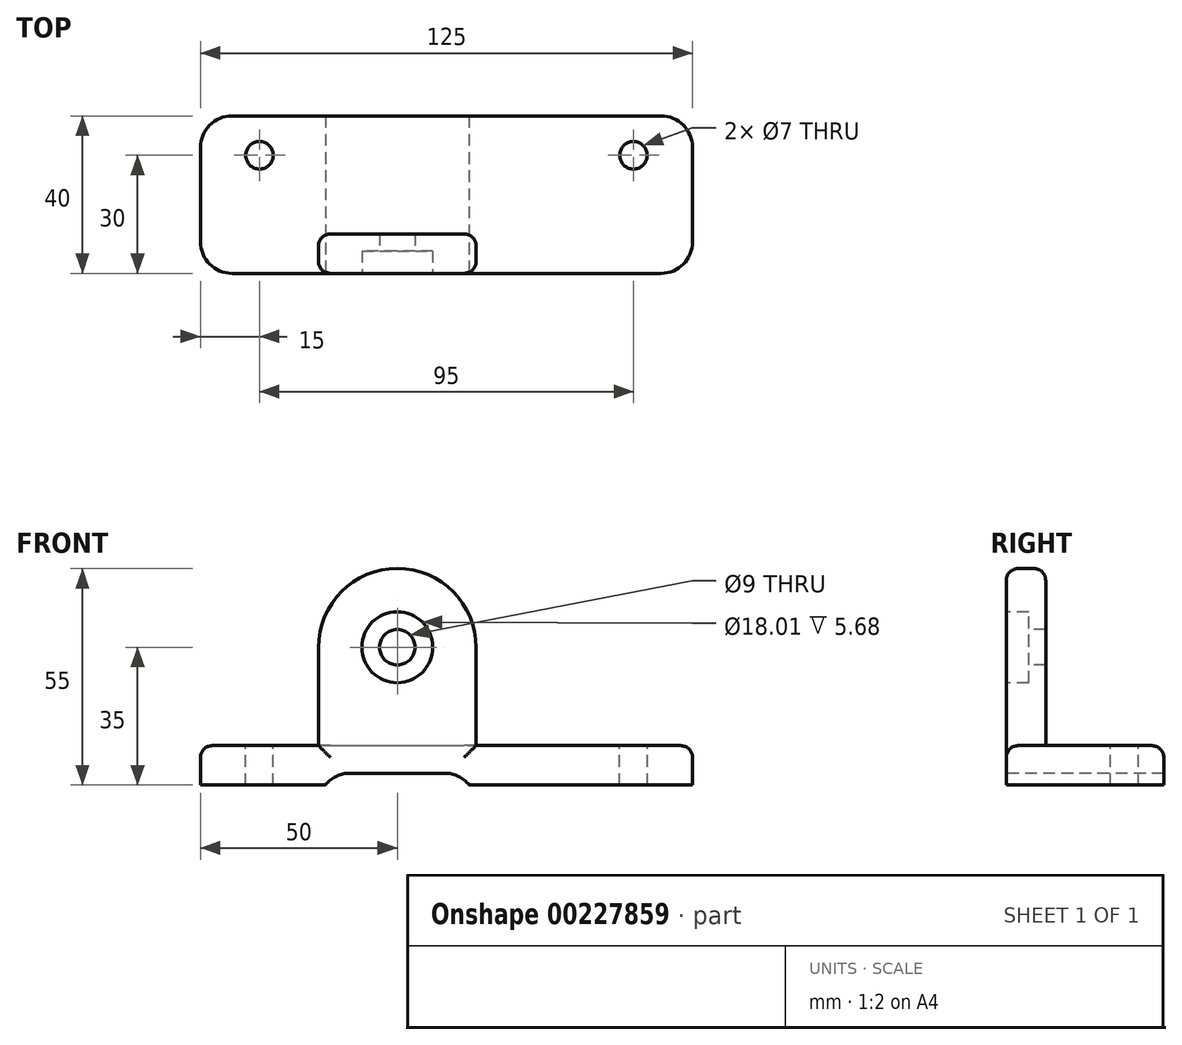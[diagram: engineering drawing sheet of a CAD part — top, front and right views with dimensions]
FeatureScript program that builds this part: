
annotation { "Feature Type Name" : "Feature", "Feature Type Description" : "" }
export const myFeature = defineFeature(function(context is Context, id is Id, definition is map)
    precondition{}
    {
        {
            var Q0;
            Q0=qCreatedBy(makeId("Top.planeOp"),FACE);
            var sketch = newSketch(context, id + "F0", { "sketchPlane" : qUnion([Q0])});
            skLineSegment(sketch, "E0.bottom", {"start": v(-62.5, 0) * mm, "end": v(62.5, 0) * mm});
            skLineSegment(sketch, "E0.top", {"start": v(-62.5, -40) * mm, "end": v(62.5, -40) * mm});
            skLineSegment(sketch, "E0.left", {"start": v(-62.5, 0) * mm, "end": v(-62.5, -40) * mm});
            skLineSegment(sketch, "E0.right", {"start": v(62.5, 0) * mm, "end": v(62.5, -40) * mm});
            skSolve(sketch);
        }
        {
            var Q0;
            Q0=makeQuery(id+"F0.imprint","IMPRINT",FACE,{"disambiguationData":[TD([[makeQuery(id+"F0.imprint","IMPRINT",EDGE,{"derivedFrom":sQuery(id+"F0.wireOp",EDGE,"E0.bottom")}),-1.0]])]});
            extrude(context, id + "F1", {"entities" : qUnion([Q0]), "depth" : 10 * mm});
        }
        {
            var Q0;
            Q0=makeQuery(id+"F1.opExtrude","SWEPT_FACE",FACE,{"disambiguationData":[OSD([sQuery(id+"F0.wireOp",EDGE,"E0.top")])]});
            var sketch = newSketch(context, id + "F2", { "sketchPlane" : qUnion([Q0])});
            skPoint(sketch, "E1.centerSnap0", {"position": v(0, 10) * mm});
            skArc(sketch, "E2", {"start": v(7.5, 35) * mm, "mid": v(-12.5, 55) * mm, "end": v(-32.5, 35) * mm});
            skLineSegment(sketch, "E3", {"start": v(-32.5, 35) * mm, "end": v(-32.5, 10) * mm});
            skLineSegment(sketch, "E4", {"start": v(7.5, 35) * mm, "end": v(7.5, 10) * mm});
            skLineSegment(sketch, "E5", {"start": v(7.5, 10) * mm, "end": v(-32.5, 10) * mm});
            skSolve(sketch);
        }
        {
            var Q0;
            Q0=makeQuery(id+"F2.imprint","IMPRINT",FACE,{"disambiguationData":[TD([[makeQuery(id+"F2.imprint","IMPRINT",EDGE,{"derivedFrom":sQuery(id+"F2.wireOp",EDGE,"E2")}),1.0]])]});
            extrude(context, id + "F3", {"entities" : qUnion([Q0]), "operationType" : NewBodyOperationType.ADD, "oppositeDirection" : true, "depth" : 10 * mm});
        }
        {
            var Q0;
            Q0=makeQuery(id+"F3.boolean.opBoolean","MERGE",FACE,{"derivedFrom":[makeQuery(id+"F1.opExtrude","SWEPT_FACE",FACE,{"disambiguationData":[OSD([sQuery(id+"F0.wireOp",EDGE,"E0.top")])]}),makeQuery(id+"F3.opExtrude","CAP_FACE",FACE,{"disambiguationData":[OSD([sQuery(id+"F2.wireOp",EDGE,"E2"),sQuery(id+"F2.wireOp",EDGE,"E3"),sQuery(id+"F2.wireOp",EDGE,"E4"),sQuery(id+"F2.wireOp",EDGE,"E5")])],"isStart":true})]});
            var sketch = newSketch(context, id + "F4", { "sketchPlane" : qUnion([Q0])});
            skPoint(sketch, "E6", {"position": v(-12.5, 35) * mm});
            skPoint(sketch, "E6.positionSnap0", {"position": v(-12.5, 55) * mm});
            skSolve(sketch);
        }
        {
            var Q0;
            Q0=sQuery(id+"F4.wireOp",VERTEX,"E6");
            var Q1;
            Q1=makeQuery(id+"F1.opExtrude","SWEPT_BODY",BODY,{"disambiguationData":[OSD([sQuery(id+"F0.wireOp",EDGE,"E0.bottom"),sQuery(id+"F0.wireOp",EDGE,"E0.top"),sQuery(id+"F0.wireOp",EDGE,"E0.left"),sQuery(id+"F0.wireOp",EDGE,"E0.right")])]});
            hole(context, id + "F5", {"style" : HoleStyle.C_BORE, "endStyle" : HoleEndStyle.THROUGH, "holeDiameter" : 9 * mm, "cBoreDiameter" : 18.01 * mm, "cBoreDepth" : 5.68 * mm, "locations" : qUnion([Q0]), "scope" : qUnion([Q1]), "isTappedThrough" : true});
        }
        {
            var Q0;
            Q0=makeQuery(id+"F1.opExtrude","CAP_FACE",FACE,{"disambiguationData":[OSD([sQuery(id+"F0.wireOp",EDGE,"E0.bottom"),sQuery(id+"F0.wireOp",EDGE,"E0.top"),sQuery(id+"F0.wireOp",EDGE,"E0.left"),sQuery(id+"F0.wireOp",EDGE,"E0.right")])],"isStart":false});
            var sketch = newSketch(context, id + "F6", { "sketchPlane" : qUnion([Q0])});
            skPoint(sketch, "E7", {"position": v(-47.5, -10) * mm});
            skPoint(sketch, "E8", {"position": v(103.03, -7.46) * mm});
            skPoint(sketch, "E9", {"position": v(47.5, -10) * mm});
            skSolve(sketch);
        }
        {
            var Q0;
            Q0=sQuery(id+"F6.wireOp",VERTEX,"E7");
            var Q1;
            Q1=sQuery(id+"F6.wireOp",VERTEX,"E9");
            var Q2;
            Q2=makeQuery(id+"F1.opExtrude","SWEPT_BODY",BODY,{"disambiguationData":[OSD([sQuery(id+"F0.wireOp",EDGE,"E0.bottom"),sQuery(id+"F0.wireOp",EDGE,"E0.top"),sQuery(id+"F0.wireOp",EDGE,"E0.left"),sQuery(id+"F0.wireOp",EDGE,"E0.right")])]});
            hole(context, id + "F7", {"style" : HoleStyle.SIMPLE, "endStyle" : HoleEndStyle.THROUGH, "holeDiameter" : 7 * mm, "locations" : qUnion([Q0, Q1]), "scope" : qUnion([Q2]), "isTappedThrough" : true});
        }
        {
            var Q0;
            Q0=makeQuery(id+"F3.boolean.opBoolean","MERGE",FACE,{"derivedFrom":[makeQuery(id+"F1.opExtrude","SWEPT_FACE",FACE,{"disambiguationData":[OSD([sQuery(id+"F0.wireOp",EDGE,"E0.top")])]}),makeQuery(id+"F3.opExtrude","CAP_FACE",FACE,{"disambiguationData":[OSD([sQuery(id+"F2.wireOp",EDGE,"E2"),sQuery(id+"F2.wireOp",EDGE,"E3"),sQuery(id+"F2.wireOp",EDGE,"E4"),sQuery(id+"F2.wireOp",EDGE,"E5")])],"isStart":true})]});
            var sketch = newSketch(context, id + "F8", { "sketchPlane" : qUnion([Q0])});
            skLineSegment(sketch, "E10.bottom", {"start": v(-32.5, 0) * mm, "end": v(7.5, 0) * mm});
            skLineSegment(sketch, "E10.top", {"start": v(-24.5, 3) * mm, "end": v(-0.5, 3) * mm});
            skLineSegment(sketch, "E10.left", {"start": v(-32.5, -5) * mm, "end": v(-32.5, 0) * mm});
            skLineSegment(sketch, "E10.right", {"start": v(7.5, -5) * mm, "end": v(7.5, 0) * mm});
            skPoint(sketch, "E11.visualSharp", {"position": v(-32.5, 3) * mm});
            skArc(sketch, "E11.filletArc", {"start": v(-24.5, 3) * mm, "mid": v(-30.16, 0.66) * mm, "end": v(-32.5, -5) * mm});
            skPoint(sketch, "E12.visualSharp", {"position": v(7.5, 3) * mm});
            skArc(sketch, "E12.filletArc", {"start": v(7.5, -5) * mm, "mid": v(5.16, 0.66) * mm, "end": v(-0.5, 3) * mm});
            skSolve(sketch);
        }
        {
            var Q0;
            {var subQ5=sQuery(id+"F8.wireOp",EDGE,"E10.top");Q0=makeQuery(id+"F8.imprint","IMPRINT",FACE,{"disambiguationData":[TD([[makeQuery(id+"F8.imprint","IMPRINT",EDGE,{"derivedFrom":subQ5}),-1.0]])]});}
            extrude(context, id + "F9", {"entities" : qUnion([Q0]), "operationType" : NewBodyOperationType.REMOVE, "oppositeDirection" : true, "depth" : 40 * mm});
        }
        {
            var Q0;
            Q0=makeQuery(id+"F1.opExtrude","SWEPT_EDGE",EDGE,{"disambiguationData":[OSD([sQuery(id+"F0.wireOp",EDGE,"E0.top"),sQuery(id+"F0.wireOp",EDGE,"E0.right")])]});
            var Q1;
            Q1=makeQuery(id+"F1.opExtrude","SWEPT_EDGE",EDGE,{"disambiguationData":[OSD([sQuery(id+"F0.wireOp",EDGE,"E0.bottom"),sQuery(id+"F0.wireOp",EDGE,"E0.right")])]});
            var Q2;
            Q2=makeQuery(id+"F1.opExtrude","SWEPT_EDGE",EDGE,{"disambiguationData":[OSD([sQuery(id+"F0.wireOp",EDGE,"E0.bottom"),sQuery(id+"F0.wireOp",EDGE,"E0.left")])]});
            var Q3;
            Q3=makeQuery(id+"F1.opExtrude","SWEPT_EDGE",EDGE,{"disambiguationData":[OSD([sQuery(id+"F0.wireOp",EDGE,"E0.top"),sQuery(id+"F0.wireOp",EDGE,"E0.left")])]});
            fillet(context, id + "F10", {"entities" : qUnion([Q0, Q1, Q2, Q3]), "radius" : 8 * mm, "tangentPropagation" : true, "allowEdgeOverflow" : false});
        }
        {
            var Q0;
            {var subQ1=sQuery(id+"F0.wireOp",EDGE,"E0.left");var subQ2=sQuery(id+"F0.wireOp",EDGE,"E0.top");Q0=makeQuery(id+"F3.boolean.opBoolean","SPLIT",EDGE,{"disambiguationData":[TD([makeQuery(id+"F1.opExtrude","SWEPT_FACE",FACE,{"disambiguationData":[OSD([subQ1])]})])],"derivedFrom":makeQuery(id+"F1.opExtrude","CAP_EDGE",EDGE,{"disambiguationData":[OSD([subQ2])],"isStart":false})});}
            var Q1;
            Q1=makeQuery(id+"F3.opExtrude","CAP_EDGE",EDGE,{"disambiguationData":[OSD([sQuery(id+"F2.wireOp",EDGE,"E4")])],"isStart":true});
            var Q2;
            Q2=makeQuery(id+"F3.opExtrude","CAP_EDGE",EDGE,{"disambiguationData":[OSD([sQuery(id+"F2.wireOp",EDGE,"E4")])],"isStart":false});
            var Q3;
            Q3=makeQuery(id+"F3.opExtrude","CAP_EDGE",EDGE,{"disambiguationData":[OSD([sQuery(id+"F2.wireOp",EDGE,"E5")])],"isStart":false});
            fillet(context, id + "F11", {"entities" : qUnion([Q0, Q1, Q2, Q3]), "radius" : 3 * mm, "tangentPropagation" : true, "allowEdgeOverflow" : false});
        }
    });
